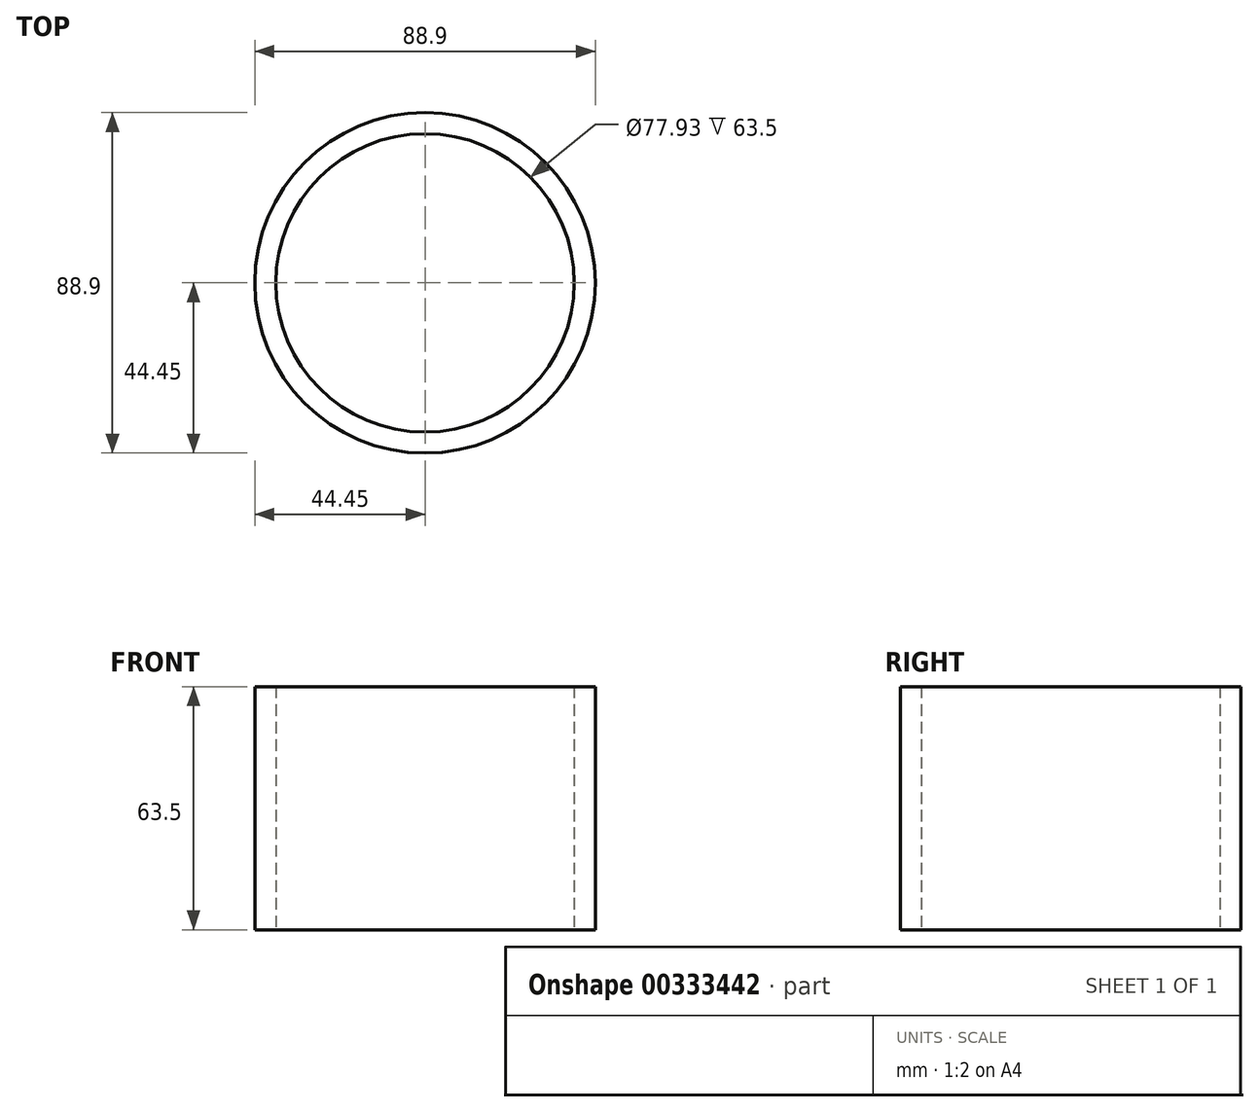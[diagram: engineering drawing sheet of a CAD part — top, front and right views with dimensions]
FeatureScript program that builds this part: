
annotation { "Feature Type Name" : "Feature", "Feature Type Description" : "" }
export const myFeature = defineFeature(function(context is Context, id is Id, definition is map)
    precondition{}
    {
        {
            var Q0;
            Q0=qCreatedBy(makeId("Top.planeOp"),FACE);
            var sketch = newSketch(context, id + "F0", { "sketchPlane" : qUnion([Q0])});
            skCircle(sketch, "E0", {"center": v(0, 0) * mm, "radius": 44.45 * mm});
            skCircle(sketch, "E1", {"center": v(0, 0) * mm, "radius": 38.96 * mm});
            skSolve(sketch);
        }
        {
            var Q0;
            Q0=makeQuery(id+"F0.imprint","IMPRINT",FACE,{"disambiguationData":[TD([[makeQuery(id+"F0.imprint","IMPRINT",EDGE,{"derivedFrom":sQuery(id+"F0.wireOp",EDGE,"E0")}),1.0]])]});
            extrude(context, id + "F1", {"entities" : qUnion([Q0]), "depth" : 63.5 * mm});
        }
    });
